# Revit family: Reece_Shower_Milli_Marq Edit_Single Rail Shower
name_source: partatom
category: Plumbing Fixtures
revit_build: Autodesk Revit 2018 (Build: 20181011_1500(x64)
units: mm (PartAtom-declared; Revit-internal decimal feet)

## family parameters
Cut with Voids When Loaded = Yes
Host = Face
Part Type = Normal
Room Calculation Point = Yes
Round Connector Dimension = Use Diameter
Shared = Yes

## types (12) — shared parameters
Reece_Detail_Additional = Twin Rail Shower
Reece_Product_Brand = Milli
Reece_Product_Mount = Wall Mounted
Reece_Product_Sub Brand = Marq Edit
Reece_Product_Type = Shower
Reece_Product_Web Page = https://www.reece.com.au
Reece_Shower_Inlet = 12 mm  [stored 0.0393701 ft]
zero-valued in all types: Default Elevation

## per-type parameters (varying)
| type | Reece_Material_Colour | Reece_Material_Main | Reece_Material_Secondary | Reece_Product_Description | Reece_Product_Number |
| Polished Chrome_4 Star | Reece_Plastic_White | Reece_Brass_Chrome | Reece_Brass_Chrome_Knurl Pattern | Milli Marq Edit Single Rail Shower Chrome (4 Star) | 21996 |
| Brushed Nickel_4 Star | Reece_Plastic_White | Reece_Brass_Brushed Nickel | Reece_Brass_Brushed Nickel_Knurl Pattern | Milli Marq Edit Single Rail Shower Brushed Nickel (4 Star) | 21998 |
| Brushed Bronze_4 Star | Reece_Plastic_White | Reece_PVD_Brushed Bronze | Reece_PVD_Brushed Bronze_Knurl Pattern | Milli Marq Edit Single Rail Shower Brushed Bronze (4 Star) | 22001 |
| Brushed Gold_4 Star | Reece_Plastic_White | Reece_PVD_Brushed Gold | Reece_PVD_Brushed Gold_Knurl Pattern | Milli Marq Edit Single Rail Shower Brushed Gold (4 Star) | 21999 |
| Matte Black_4 Star | Reece_Plastic_ABS_Matte Black | Reece_Brass_Matte Black | Reece_Brass_Matte Black_Knurl Pattern | Milli Marq Edit Single Rail Shower Matte Black (4 Star) | 21997 |
| Brushed Gunmetal_4 Star | Reece_Plastic_ABS_Matte Black | Reece_Brass_Brushed Gunmetal | Reece_Brass_Brushed Gunmetal_Knurl Pattern | Milli Marq Edit Single Rail Shower Brushed Gunmetal (4 Star) | 22000 |
| Brushed Gunmetal_3 Star | Reece_Plastic_ABS_Matte Black | Reece_Brass_Brushed Gunmetal | Reece_Brass_Brushed Gunmetal_Knurl Pattern | Milli Marq Edit Single Rail Shower Brushed Gunmetal (3 Star) | 21970 |
| Matte Black_3 Star | Reece_Plastic_ABS_Matte Black | Reece_Brass_Matte Black | Reece_Brass_Matte Black_Knurl Pattern | Milli Marq Edit Single Rail Shower Matte Black (3 Star) | 21967 |
| Polished Chrome_3 Star | Reece_Plastic_White | Reece_Brass_Chrome | Reece_Brass_Chrome_Knurl Pattern | Milli Marq Edit Single Rail Shower Chrome (3 Star) | 21966 |
| Brushed Nickel_3 Star | Reece_Plastic_White | Reece_Brass_Brushed Nickel | Reece_Brass_Brushed Nickel_Knurl Pattern | Milli Marq Edit Single Rail Shower Brushed Nickel (3 Star) | 21968 |
| Brushed Gold_3 Star | Reece_Plastic_White | Reece_PVD_Brushed Gold | Reece_PVD_Brushed Gold_Knurl Pattern | Milli Marq Edit Single Rail Shower Brushed Gold (3 Star) | 21969 |
| Brushed Bronze_3 Star | Reece_Plastic_White | Reece_PVD_Brushed Bronze | Reece_PVD_Brushed Bronze_Knurl Pattern | Milli Marq Edit Single Rail Shower Brushed Bronze (3 Star) | 21971 |

note: [stored X ft] marks values corroborated as IEEE doubles in the binary element streams (Revit-internal decimal feet)

## geometry (parser evidence)
native form markers: Sweep x4
no freeform markers — native parametric forms only
